# Revit family: LO-100
name_source: partatom
category: Mechanical Equipment
revit_build: Autodesk Revit 2018 (Build: 20190510_1515(x64)
units: mm (PartAtom-declared; Revit-internal decimal feet)

## family parameters
Always vertical = Yes
Cut with Voids When Loaded = No
OmniClass Number = 23.75.00.00
OmniClass Title = Climate Control (HVAC)
Part Type = Normal
Room Calculation Point = No
Round Connector Dimension = Use Diameter
Shared = No
Work Plane-Based = No

## types (10) — shared parameters
B = 0' - 8 1/2"
C = 0' - 1 7/8"
F = 0' - 11"
H = 0' - 7"
Hz = 60
I = 0' - 0 1/2"

## per-type parameters (varying)
| type | A | D | E | G | GPH. Oil No.2 / No.4 | J | Model LO-101E | Model LO-102E | Model LO-103E | Model LO-104E | Model LO-105E | Model LO-106E | Motor HP | Motor RPM | PSI | Phase | Volts | Weight (lbs.) |
| LO-101E_100PSI | 1' - 3 5/8" | 1' - 5 1/4" | 0' - 7 19/32" | 0' - 10" | 23 / 24 | 0' - 1 5/8" | Yes | No | No | No | No | No | 1/3 | 1725 | 100.00 psi | 1 | 115, 208, 230 | 35.50 lbm |
| LO-102E_100PSI | 1' - 4 1/8" | 1' - 5 1/4" | 0' - 7 9/16" | 10' - 0" | 51 / 54 | 0' - 1 1/8" | No | Yes | No | No | No | No | 1/3 | 1725 | 100.00 psi | 1 | 115, 208, 230 | 36.50 lbm |
| LO-103E_100PSI | 1' - 4 1/8" | 1' - 5 1/4" | 0' - 7 9/16" | 0' - 10" | 89 / 96 | 0' - 1 1/8" | No | No | Yes | No | No | No | 1/3 | 1725 | 100.00 psi | 1 | 115, 208, 230 | 36.30 lbm |
| LO-104E_100PSI | 1' - 3 7/8" | 1' - 5 1/4" | 0' - 7 9/16" | 0' - 8 5/8" | 150 / 161 | 0' - 1 3/8" | No | No | No | Yes | No | No | 1/2 | 1725 | 100.00 psi | 3 | 208, 230, 460 | 36.60 lbm |
| LO-105E_50PSI | 1' - 3 3/4" | 1' - 5 3/16" | 0' - 7 9/16" | 0' - 8 5/8" | 328 / 344 | 0' - 1 7/16" | No | No | No | No | Yes | No | 3/4 | 1725 | 50.00 psi | 3 | 208, 230, 460 | 41.80 lbm |
| LO-106E_100PSI | 1' - 4 7/16" | 1' - 5 3/4" | 0' - 7 9/16" | 0' - 8 5/8" | 277 / 285 | 0' - 1 5/16" | No | No | No | No | No | Yes | 1 | 1760 | 100.00 psi | 3 | 208, 230, 460 | 46.00 lbm |
| LO-101E_50PSI | 1' - 3 5/8" | 1' - 5 1/4" | 0' - 7 19/32" | 0' - 10" | 24 / 25 | 0' - 1 5/8" | Yes | No | No | No | No | No | 1/3 | 1725 | 50.00 psi | 1 | 115, 208, 230 | 35.50 lbm |
| LO-102E_50PSI | 1' - 4 1/8" | 1' - 5 1/4" | 0' - 7 9/16" | 10' - 0" | 54 / 56 | 0' - 1 1/8" | No | Yes | No | No | No | No | 1/3 | 1725 | 50.00 psi | 1 | 115, 208, 230 | 36.50 lbm |
| LO-103E_50PSI | 1' - 4 1/8" | 1' - 5 1/4" | 0' - 7 9/16" | 0' - 10" | 97 / 100 | 0' - 1 1/8" | No | No | Yes | No | No | No | 1/3 | 1725 | 50.00 psi | 1 | 115, 208, 230 | 36.30 lbm |
| LO-104E_50PSI | 1' - 3 7/8" | 1' - 5 1/4" | 0' - 7 9/16" | 0' - 8 5/8" | 163 / 169 | 0' - 1 3/8" | No | No | No | Yes | No | No | 1/2 | 1725 | 50.00 psi | 3 | 208, 230, 460 | 36.60 lbm |

## geometry (parser evidence)
native form markers: Sweep x3
no freeform markers — native parametric forms only
